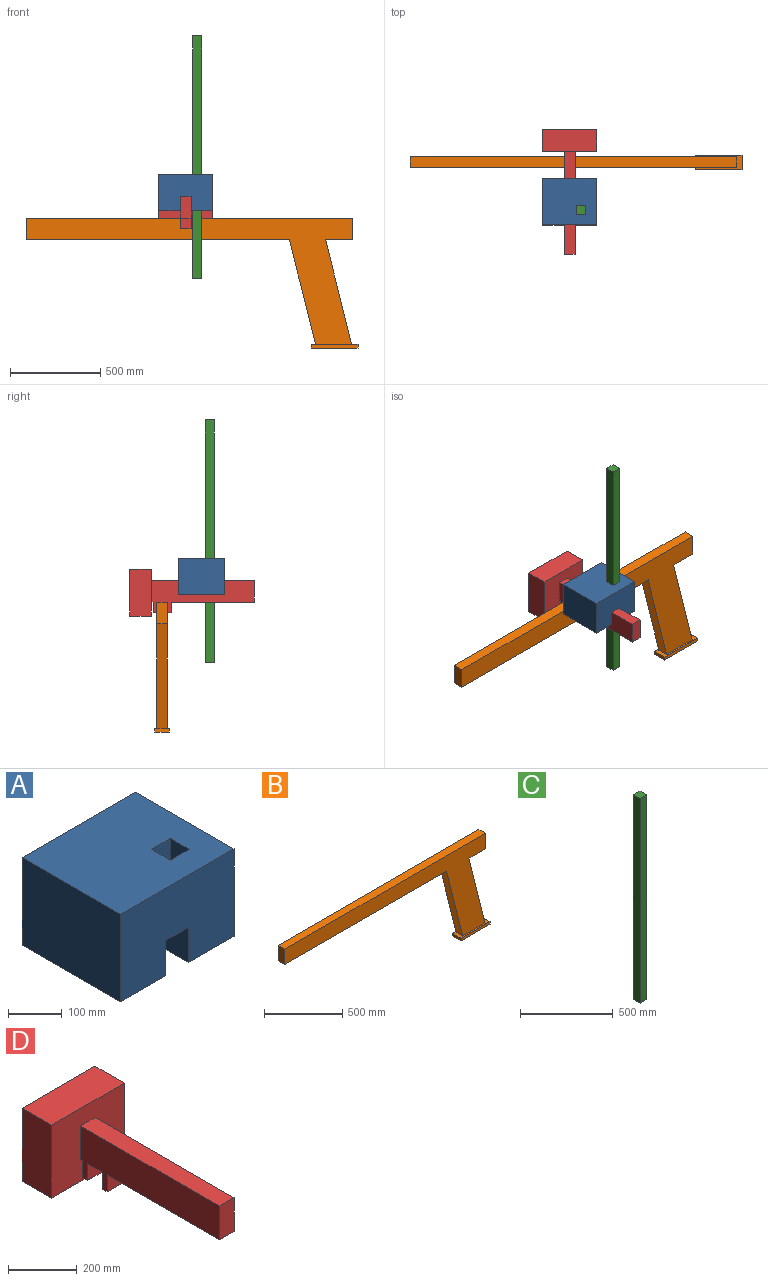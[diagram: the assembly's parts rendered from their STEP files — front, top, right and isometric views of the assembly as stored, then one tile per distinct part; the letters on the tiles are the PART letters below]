
ASSEMBLY  parts=4 mates=6
PART A: 14 faces, bbox 300x260x200 mm
  f0: plane 300x200mm, normal (0,1,0), area 55179.1mm2, adj f2,f3,f4,f5,f6,f7,f8,f9
  f1: plane 300x200mm, normal (0,-1,0), area 55179.1mm2, adj f2,f3,f4,f5,f6,f7,f8,f9
  f2: plane 260x120mm, normal (0,0,-1), area 31200mm2, adj f0,f1,f6,f8
  f3: plane 300x260mm, normal (0,0,1), area 75500mm2, adj f0,f1,f5,f6,f10,f11,f12,f13
  f4: plane 260x120mm, normal (0,0,-1), area 28700mm2, adj f0,f1,f5,f9,f10,f11,f12,f13
  f5: plane 260x200mm, normal (1,0,0), area 52000mm2, adj f0,f1,f3,f4
  f6: plane 260x200mm, normal (-1,0,0), area 52000mm2, adj f0,f1,f2,f3
  f7: plane 260x60mm, normal (0,0,-1), area 15600mm2, adj f0,f1,f8,f9
  f8: plane 260x80.35mm, normal (1,0,0), area 20890.7mm2, adj f0,f1,f2,f7
  f9: plane 260x80.35mm, normal (-1,0,0), area 20890.7mm2, adj f0,f1,f4,f7
  f10: plane 200x50mm, normal (1,0,0), area 10000mm2, adj f3,f4,f11,f13
  f11: plane 200x50mm, normal (0,1,0), area 10000mm2, adj f3,f4,f10,f12
  f12: plane 200x50mm, normal (-1,0,0), area 10000mm2, adj f3,f4,f11,f13
  f13: plane 200x50mm, normal (0,-1,0), area 10000mm2, adj f3,f4,f10,f12
PART B: 15 faces, bbox 1840x80x720 mm
  f0: plane 260x20mm, normal (0,-1,0), area 5200mm2, adj f1,f3,f4,f5
  f1: plane 80x20mm, normal (1,0,0), area 1600mm2, adj f0,f2,f4,f5
  f2: plane 260x20mm, normal (0,1,0), area 5200mm2, adj f1,f3,f4,f5
  f3: plane 80x20mm, normal (-1,0,0), area 1600mm2, adj f0,f2,f4,f5
  f4: plane 260x80mm, normal (0,0,1), area 8800mm2, adj f0,f1,f2,f3,f6,f7,f13,f14
  f5: plane 260x80mm, normal (0,0,-1), area 20800mm2, adj f0,f1,f2,f3
  f6: plane 580x145mm, normal (-0.97,0,-0.24), area 35871mm2, adj f4,f12,f13,f14
  f7: plane 580x145mm, normal (0.97,0,0.24), area 35871mm2, adj f4,f8,f13,f14
  f8: plane 150x60mm, normal (0,0,-1), area 9000mm2, adj f7,f9,f13,f14
  f9: plane 120x60mm, normal (1,0,0), area 7200mm2, adj f8,f10,f13,f14
  f10: plane 1810x60mm, normal (0,0,1), area 108600mm2, adj f9,f11,f13,f14
  f11: plane 120x60mm, normal (-1,0,0), area 7200mm2, adj f10,f12,f13,f14
  f12: plane 1460x60mm, normal (0,0,-1), area 87600mm2, adj f6,f11,f13,f14
  f13: plane 1810x700mm, normal (0,-1,0), area 333200mm2, adj f4,f6,f7,f8,f9,f10,f11,f12
  f14: plane 1810x700mm, normal (0,1,0), area 333200mm2, adj f4,f6,f7,f8,f9,f10,f11,f12
PART C: 6 faces, bbox 50x50x1346 mm
  f0: plane 50x50mm, normal (0,0,-1), area 2500mm2, adj f1,f3,f4,f5
  f1: plane 1346x50mm, normal (0,1,0), area 67300mm2, adj f0,f2,f4,f5
  f2: plane 50x50mm, normal (0,0,1), area 2500mm2, adj f1,f3,f4,f5
  f3: plane 1346x50mm, normal (0,-1,0), area 67300mm2, adj f0,f2,f4,f5
  f4: plane 1346x50mm, normal (1,0,0), area 67300mm2, adj f0,f1,f2,f3
  f5: plane 1346x50mm, normal (-1,0,0), area 67300mm2, adj f0,f1,f2,f3
PART D: 19 faces, bbox 300x692x260 mm
  f0: plane 60x9.06mm, normal (0,0,-1), area 543.4mm2, adj f2,f3,f8,f14
  f1: plane 571.06x60mm, normal (0,0,1), area 34263.4mm2, adj f2,f3,f9,f14
  f2: plane 571.06x180mm, normal (1,0,0), area 70926.7mm2, adj f0,f1,f4,f5,f6,f7,f8,f9
  f3: plane 571.06x180mm, normal (-1,0,0), area 70926.7mm2, adj f0,f1,f4,f5,f6,f7,f8,f9
  f4: plane 60x60mm, normal (0,1,0), area 3600mm2, adj f2,f3,f5,f12
  f5: plane 60x60mm, normal (0,0,-1), area 3600mm2, adj f2,f3,f4,f6
  f6: plane 60x60mm, normal (0,-1,0), area 3600mm2, adj f2,f3,f5,f7
  f7: plane 60x20mm, normal (0,0,-1), area 1200mm2, adj f2,f3,f6,f8
  f8: plane 60x60mm, normal (0,1,0), area 3600mm2, adj f0,f2,f3,f7
  f9: plane 120x60mm, normal (0,-1,0), area 7200mm2, adj f1,f2,f3,f10
  f10: plane 462x60mm, normal (0,0,-1), area 27720mm2, adj f2,f3,f9,f11
  f11: plane 60x60mm, normal (0,-1,0), area 3600mm2, adj f2,f3,f10,f12
  f12: plane 60x20mm, normal (0,0,-1), area 1200mm2, adj f2,f3,f4,f11
  f13: plane 300x120.94mm, normal (0,0,1), area 36283.1mm2, adj f14,f16,f17,f18
  f14: plane 300x260mm, normal (0,-1,0), area 70800mm2, adj f0,f1,f2,f3,f13,f15,f16,f17
  f15: plane 300x120.94mm, normal (0,0,-1), area 36283.1mm2, adj f14,f16,f17,f18
  f16: plane 260x120.94mm, normal (1,0,0), area 31445.4mm2, adj f13,f14,f15,f18
  f17: plane 260x120.94mm, normal (-1,0,0), area 31445.4mm2, adj f13,f14,f15,f18
  f18: plane 300x260mm, normal (0,1,0), area 78000mm2, adj f13,f15,f16,f17
PLACE A t=(-824.73,24.71,0)mm
PLACE B at identity fixed
PLACE C t=(-824.73,24.71,-166.35)mm
PLACE D t=(-824.73,0,0)mm
MATE planar C.f5 <-> A.f10  axis (-1,0,0) through (-784.73,-265.58,1056.65)mm
MATE planar A.f8 <-> D.f3  axis (1,0,0) through (-854.73,-218.81,799.83)mm
MATE planar B.f13 <-> D.f4  axis (0,-1,0) through (-551.73,-30,538.15)mm
MATE planar B.f10 <-> D.f5  axis (0,0,1) through (-805,0,720)mm
MATE planar D.f1 <-> A.f7  axis (0,0,1) through (-854.73,-512,840)mm
MATE planar C.f3 <-> A.f11  axis (0,-1,0) through (-759.73,-290.58,1056.65)mm
